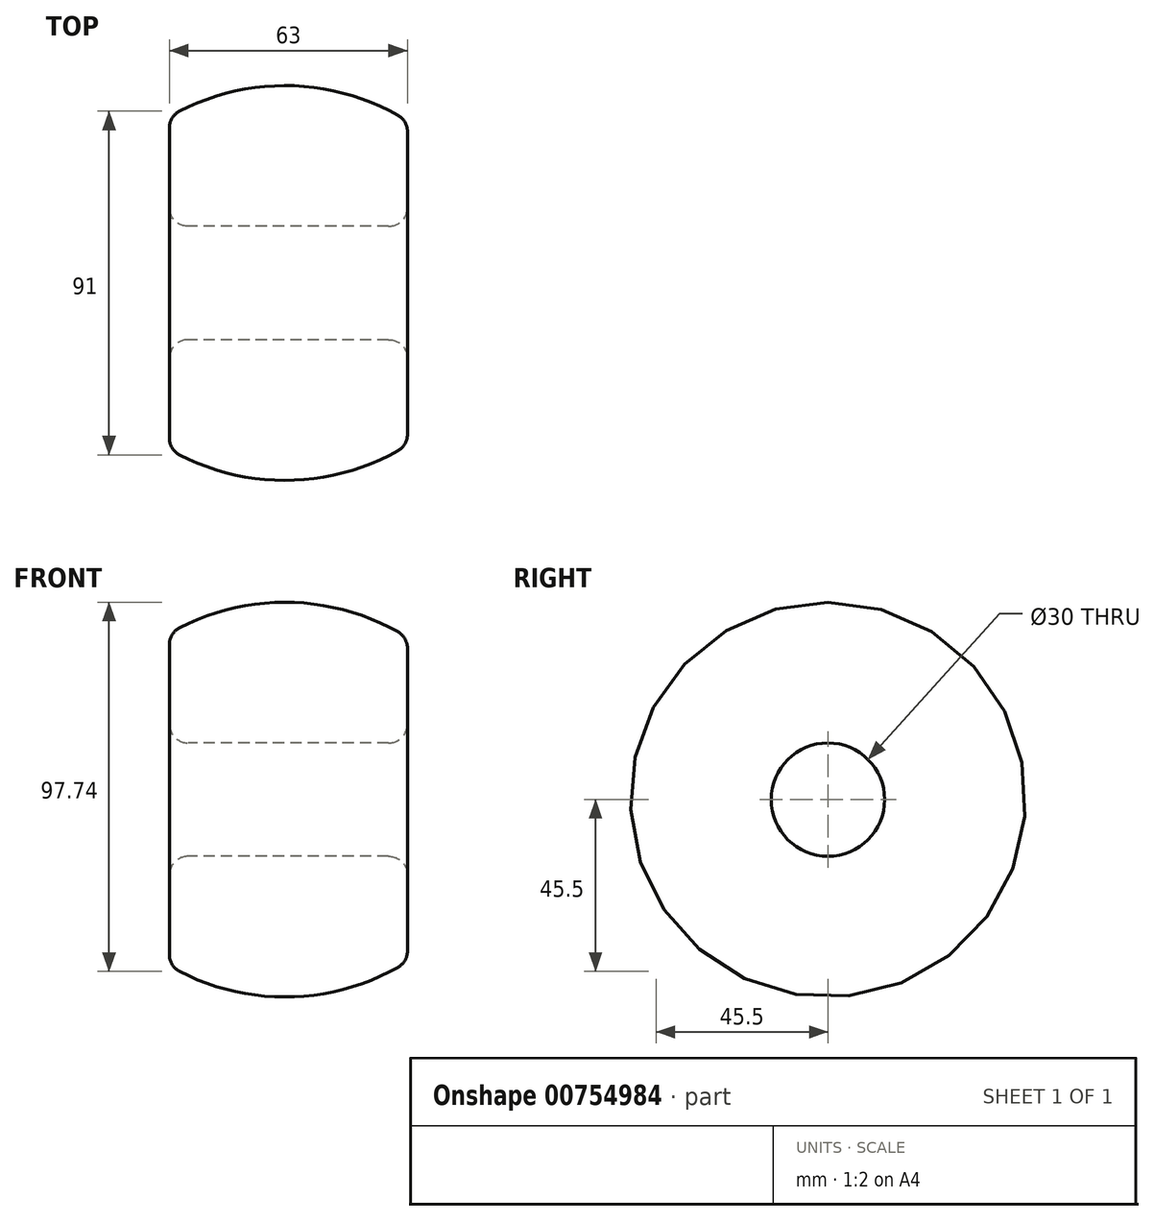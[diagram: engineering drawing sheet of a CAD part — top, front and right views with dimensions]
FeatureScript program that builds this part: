
annotation { "Feature Type Name" : "Feature", "Feature Type Description" : "" }
export const myFeature = defineFeature(function(context is Context, id is Id, definition is map)
    precondition{}
    {
        {
            var Q0;
            Q0=qCreatedBy(makeId("Top.planeOp"),FACE);
            var sketch = newSketch(context, id + "F0", { "sketchPlane" : qUnion([Q0])});
            skLineSegment(sketch, "E0", {"start": v(-65.45, 0) * mm, "end": v(206.13, 0) * mm});
            skLineSegment(sketch, "E1.top", {"start": v(-0.5, 15) * mm, "end": v(52.5, 15) * mm});
            skLineSegment(sketch, "E1.left", {"start": v(-5.5, 41.05) * mm, "end": v(-5.5, 20) * mm});
            skLineSegment(sketch, "E1.right", {"start": v(57.5, 40.05) * mm, "end": v(57.5, 20) * mm});
            skArc(sketch, "E2", {"start": v(54.95, 44.4) * mm, "mid": v(26.22, 52.23) * mm, "end": v(-2.8, 45.5) * mm});
            skPoint(sketch, "E3.visualSharp", {"position": v(-5.5, 15) * mm});
            skArc(sketch, "E3.filletArc", {"start": v(-5.5, 20) * mm, "mid": v(-4.04, 16.46) * mm, "end": v(-0.5, 15) * mm});
            skPoint(sketch, "E4.visualSharp", {"position": v(-5.5, 44.02) * mm});
            skArc(sketch, "E4.filletArc", {"start": v(-2.8, 45.5) * mm, "mid": v(-4.77, 43.66) * mm, "end": v(-5.5, 41.05) * mm});
            skPoint(sketch, "E5.visualSharp", {"position": v(57.5, 42.89) * mm});
            skArc(sketch, "E5.filletArc", {"start": v(57.5, 40.05) * mm, "mid": v(56.81, 42.57) * mm, "end": v(54.95, 44.4) * mm});
            skPoint(sketch, "E6.visualSharp", {"position": v(57.5, 15) * mm});
            skArc(sketch, "E6.filletArc", {"start": v(52.5, 15) * mm, "mid": v(56.03, 16.46) * mm, "end": v(57.5, 20) * mm});
            skSolve(sketch);
        }
        {
            var Q0;
            Q0 = qSketchRegion(id + "F0", true);
            var Q1;
            Q1=sQuery(id+"F0.wireOp",EDGE,"E0");
            revolve(context, id + "F1", {"surfaceOperationType" : NewSurfaceOperationType.NEW, "entities" : qUnion([Q0]), "axis" : qUnion([Q1]), "revolveType" : RevolveType.FULL});
        }
    });
